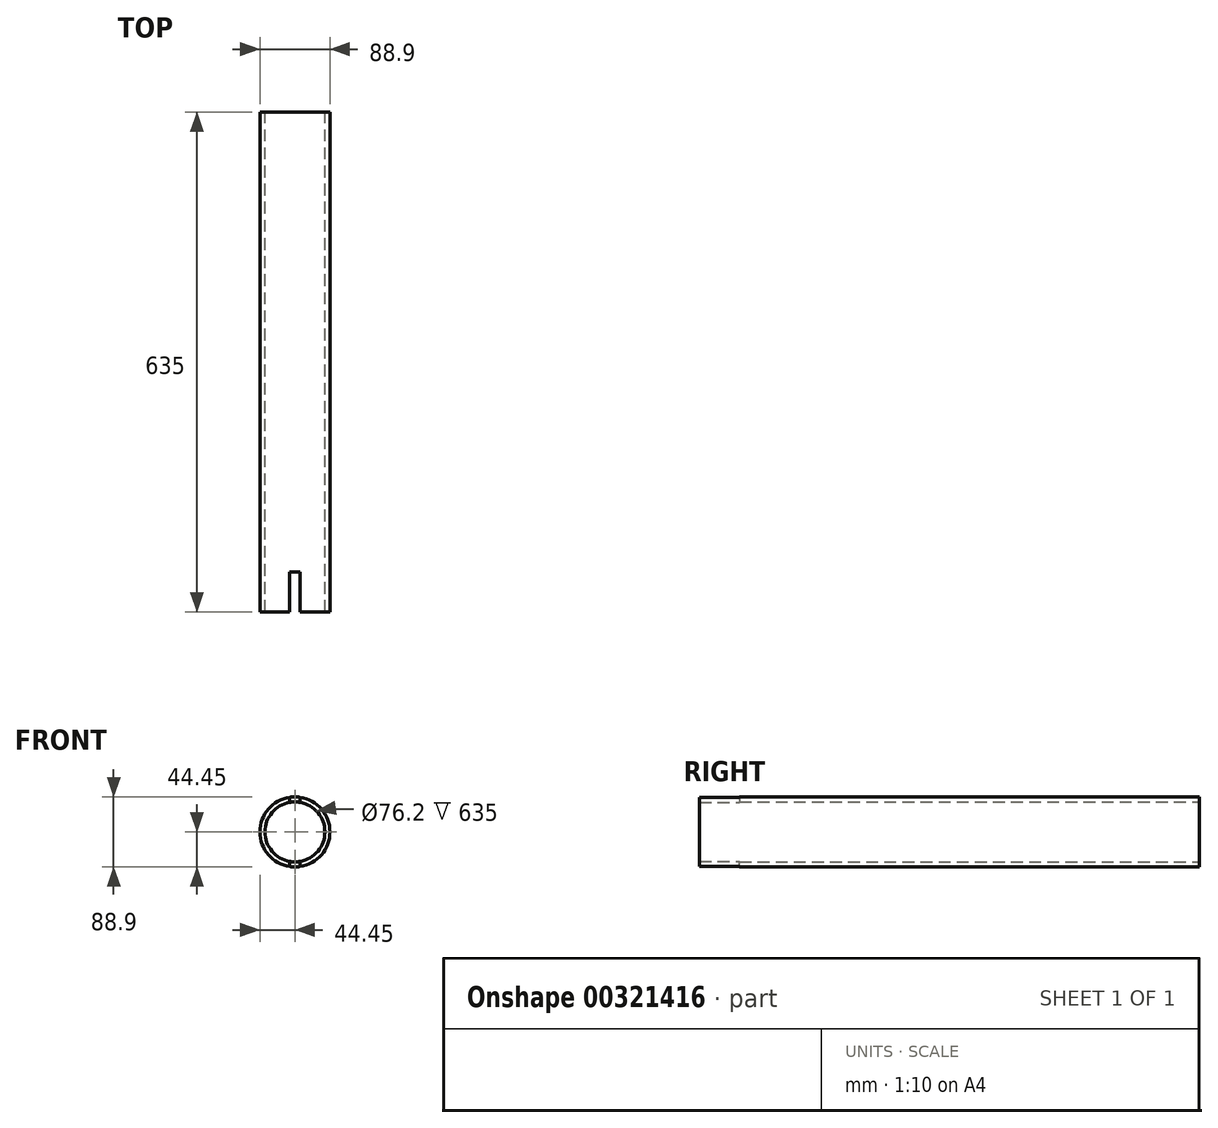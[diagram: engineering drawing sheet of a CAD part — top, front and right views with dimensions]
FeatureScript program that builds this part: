
annotation { "Feature Type Name" : "Feature", "Feature Type Description" : "" }
export const myFeature = defineFeature(function(context is Context, id is Id, definition is map)
    precondition{}
    {
        {
            var Q0;
            Q0=qCreatedBy(makeId("Front.planeOp"),FACE);
            var sketch = newSketch(context, id + "F0", { "sketchPlane" : qUnion([Q0])});
            skCircle(sketch, "E0", {"center": v(0, 0) * mm, "radius": 38.1 * mm});
            skCircle(sketch, "E1", {"center": v(0, 0) * mm, "radius": 44.45 * mm});
            skSolve(sketch);
        }
        {
            var Q0;
            Q0 = qSketchRegion(id + "F0", true);
            extrude(context, id + "F1", {"entities" : qUnion([Q0]), "endBound" : BoundingType.SYMMETRIC, "depth" : 635 * mm});
        }
        {
            var Q0;
            Q0=qCreatedBy(makeId("Top.planeOp"),FACE);
            var sketch = newSketch(context, id + "F2", { "sketchPlane" : qUnion([Q0])});
            skLineSegment(sketch, "E2.0", {"start": v(44.45, -317.5) * mm, "end": v(-44.45, -317.5) * mm});
            skLineSegment(sketch, "E3.bottom", {"start": v(-6.67, -266.7) * mm, "end": v(6.67, -266.7) * mm});
            skLineSegment(sketch, "E3.top", {"start": v(-6.67, -368.3) * mm, "end": v(6.67, -368.3) * mm});
            skLineSegment(sketch, "E3.left", {"start": v(-6.67, -266.7) * mm, "end": v(-6.67, -368.3) * mm});
            skLineSegment(sketch, "E3.right", {"start": v(6.67, -266.7) * mm, "end": v(6.67, -368.3) * mm});
            skPoint(sketch, "E3.middle", {"position": v(0, -317.5) * mm});
            skSolve(sketch);
        }
        {
            var Q0;
            Q0 = qSketchRegion(id + "F2", true);
            extrude(context, id + "F3", {"entities" : qUnion([Q0]), "operationType" : NewBodyOperationType.REMOVE, "endBound" : BoundingType.THROUGH_ALL, "depth" : 25.4 * mm});
        }
        {
            var Q0;
            {var subQ5=sQuery(id+"F2.wireOp",EDGE,"E3.bottom");Q0=makeQuery(id+"F2.imprint","IMPRINT",FACE,{"disambiguationData":[TD([[makeQuery(id+"F2.imprint","IMPRINT",EDGE,{"derivedFrom":subQ5}),-1.0]])]});}
            extrude(context, id + "F4", {"entities" : qUnion([Q0]), "operationType" : NewBodyOperationType.REMOVE, "endBound" : BoundingType.THROUGH_ALL, "oppositeDirection" : true, "depth" : 25.4 * mm});
        }
    });
